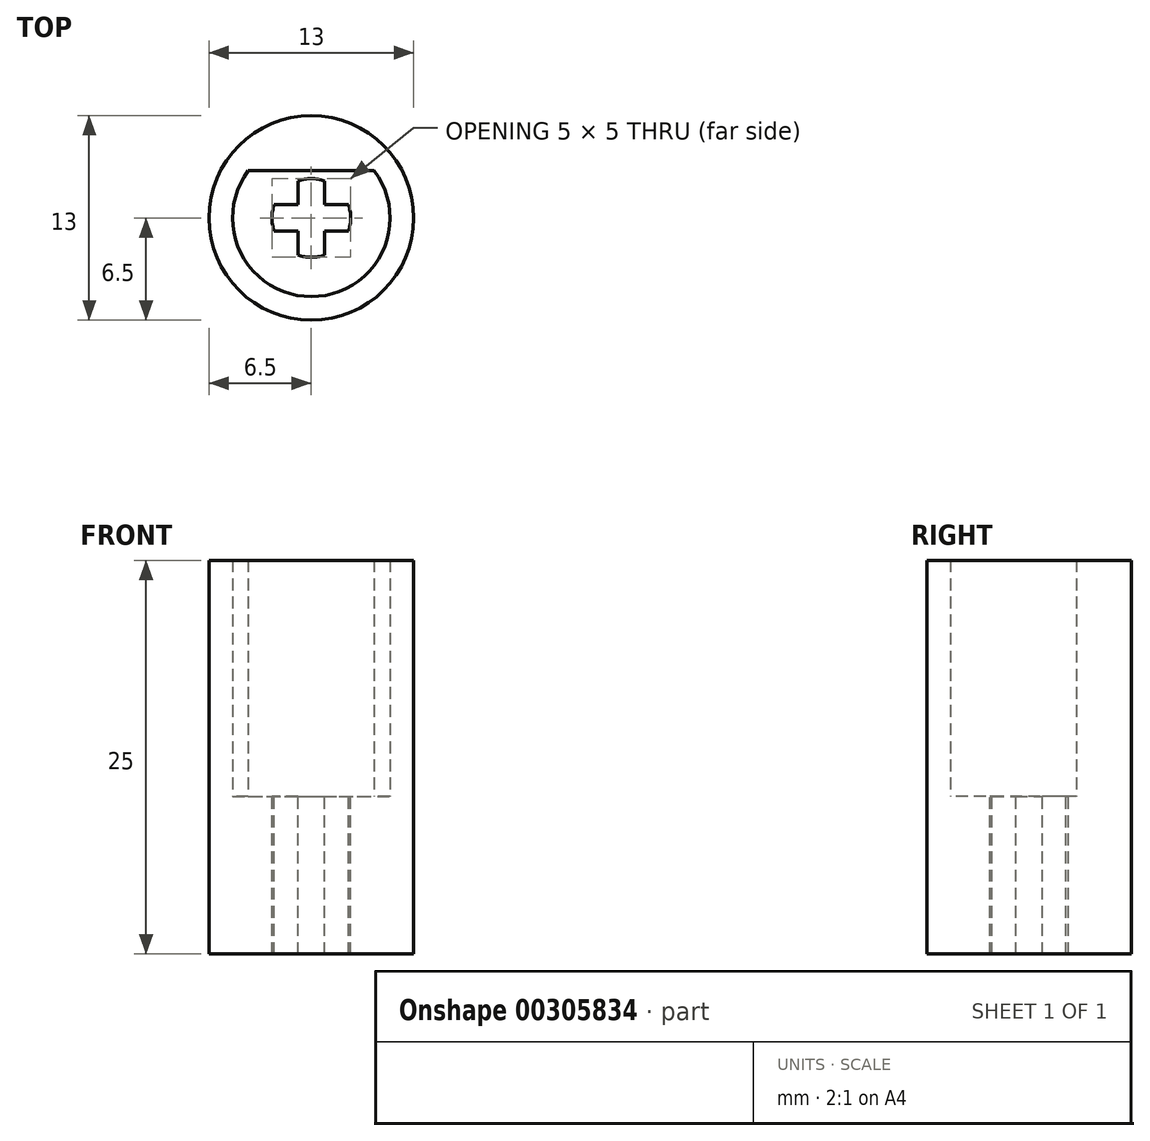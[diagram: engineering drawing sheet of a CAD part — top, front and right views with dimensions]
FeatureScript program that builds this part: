
annotation { "Feature Type Name" : "Feature", "Feature Type Description" : "" }
export const myFeature = defineFeature(function(context is Context, id is Id, definition is map)
    precondition{}
    {
        {
            var Q0;
            Q0=qCreatedBy(makeId("Top.planeOp"),FACE);
            var sketch = newSketch(context, id + "F0", { "sketchPlane" : qUnion([Q0])});
            skCircle(sketch, "E0", {"center": v(0, 0) * mm, "radius": 5 * mm});
            skLineSegment(sketch, "E1", {"start": v(-4, 3) * mm, "end": v(4, 3) * mm});
            skCircle(sketch, "E2", {"center": v(0, 0) * mm, "radius": 6.5 * mm});
            skSolve(sketch);
        }
        {
            var Q0;
            Q0=makeQuery(id+"F0.imprint","IMPRINT",FACE,{"disambiguationData":[TD([[makeQuery(id+"F0.imprint","IMPRINT",EDGE,{"derivedFrom":sQuery(id+"F0.wireOp",EDGE,"E2")}),1.0]])]});
            var Q1;
            {var subQ0=sQuery(id+"F0.wireOp",EDGE,"E1");Q1=makeQuery(id+"F0.imprint","IMPRINT",FACE,{"disambiguationData":[TD([[makeQuery(id+"F0.imprint","IMPRINT",EDGE,{"derivedFrom":subQ0}),1.0]])]});}
            extrude(context, id + "F1", {"entities" : qUnion([Q0, Q1]), "depth" : 15 * mm});
        }
        {
            var Q0;
            Q0=qCreatedBy(makeId("Top.planeOp"),FACE);
            var sketch = newSketch(context, id + "F2", { "sketchPlane" : qUnion([Q0])});
            skCircle(sketch, "E3", {"center": v(0, 0) * mm, "radius": 2.5 * mm});
            skLineSegment(sketch, "E4", {"start": v(-0.85, -2.35) * mm, "end": v(-0.85, -0.85) * mm});
            skLineSegment(sketch, "E5", {"start": v(-0.85, -0.85) * mm, "end": v(-2.35, -0.85) * mm});
            skLineSegment(sketch, "E6", {"start": v(0.85, -2.35) * mm, "end": v(0.85, -0.85) * mm});
            skLineSegment(sketch, "E7", {"start": v(0.85, -0.85) * mm, "end": v(2.35, -0.85) * mm});
            skLineSegment(sketch, "E8", {"start": v(-2.35, 0.85) * mm, "end": v(-0.85, 0.85) * mm});
            skLineSegment(sketch, "E9", {"start": v(-0.85, 2.35) * mm, "end": v(-0.85, 0.85) * mm});
            skLineSegment(sketch, "E10", {"start": v(0.85, 0.85) * mm, "end": v(0.85, 2.35) * mm});
            skLineSegment(sketch, "E11", {"start": v(0.85, 0.85) * mm, "end": v(2.35, 0.85) * mm});
            skCircle(sketch, "E12", {"center": v(0, 0) * mm, "radius": 6.5 * mm});
            skSolve(sketch);
        }
        {
            var Q0;
            Q0=makeQuery(id+"F2.imprint","IMPRINT",FACE,{"disambiguationData":[TD([[makeQuery(id+"F2.imprint","IMPRINT",EDGE,{"derivedFrom":sQuery(id+"F2.wireOp",EDGE,"E12")}),1.0]])]});
            var Q1;
            {var subQ0=sQuery(id+"F2.wireOp",EDGE,"E4");Q1=makeQuery(id+"F2.imprint","IMPRINT",FACE,{"disambiguationData":[TD([[makeQuery(id+"F2.imprint","IMPRINT",EDGE,{"derivedFrom":subQ0}),1.0]])]});}
            var Q2;
            {var subQ0=sQuery(id+"F2.wireOp",EDGE,"E6");Q2=makeQuery(id+"F2.imprint","IMPRINT",FACE,{"disambiguationData":[TD([[makeQuery(id+"F2.imprint","IMPRINT",EDGE,{"derivedFrom":subQ0}),-1.0]])]});}
            var Q3;
            {var subQ0=sQuery(id+"F2.wireOp",EDGE,"E8");Q3=makeQuery(id+"F2.imprint","IMPRINT",FACE,{"disambiguationData":[TD([[makeQuery(id+"F2.imprint","IMPRINT",EDGE,{"derivedFrom":subQ0}),1.0]])]});}
            var Q4;
            {var subQ0=sQuery(id+"F2.wireOp",EDGE,"E10");Q4=makeQuery(id+"F2.imprint","IMPRINT",FACE,{"disambiguationData":[TD([[makeQuery(id+"F2.imprint","IMPRINT",EDGE,{"derivedFrom":subQ0}),-1.0]])]});}
            extrude(context, id + "F3", {"entities" : qUnion([Q0, Q1, Q2, Q3, Q4]), "operationType" : NewBodyOperationType.ADD, "oppositeDirection" : true, "depth" : 10 * mm});
        }
    });
